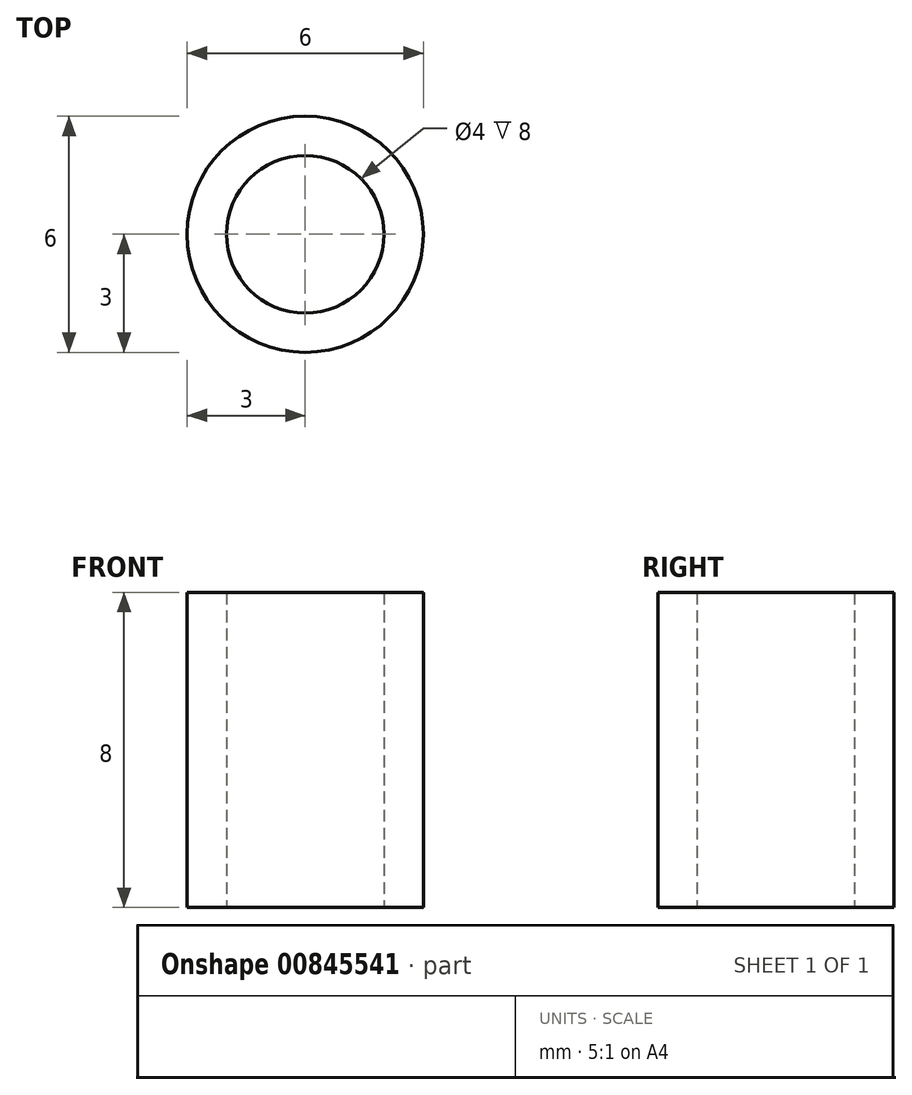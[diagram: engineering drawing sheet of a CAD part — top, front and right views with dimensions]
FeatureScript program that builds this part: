
annotation { "Feature Type Name" : "Feature", "Feature Type Description" : "" }
export const myFeature = defineFeature(function(context is Context, id is Id, definition is map)
    precondition{}
    {
        {
            var Q0;
            Q0=qCreatedBy(makeId("Top.planeOp"),FACE);
            var sketch = newSketch(context, id + "F0", { "sketchPlane" : qUnion([Q0])});
            skCircle(sketch, "E0", {"center": v(0, 0) * mm, "radius": 3 * mm});
            skCircle(sketch, "E1", {"center": v(0, 0) * mm, "radius": 2 * mm});
            skSolve(sketch);
        }
        {
            var Q0;
            Q0=makeQuery(id+"F0.imprint","IMPRINT",FACE,{"disambiguationData":[TD([[makeQuery(id+"F0.imprint","IMPRINT",EDGE,{"derivedFrom":sQuery(id+"F0.wireOp",EDGE,"E0")}),1.0]])]});
            extrude(context, id + "F1", {"entities" : qUnion([Q0]), "depth" : 8 * mm, "offsetDistance" : 25 * mm});
        }
    });
